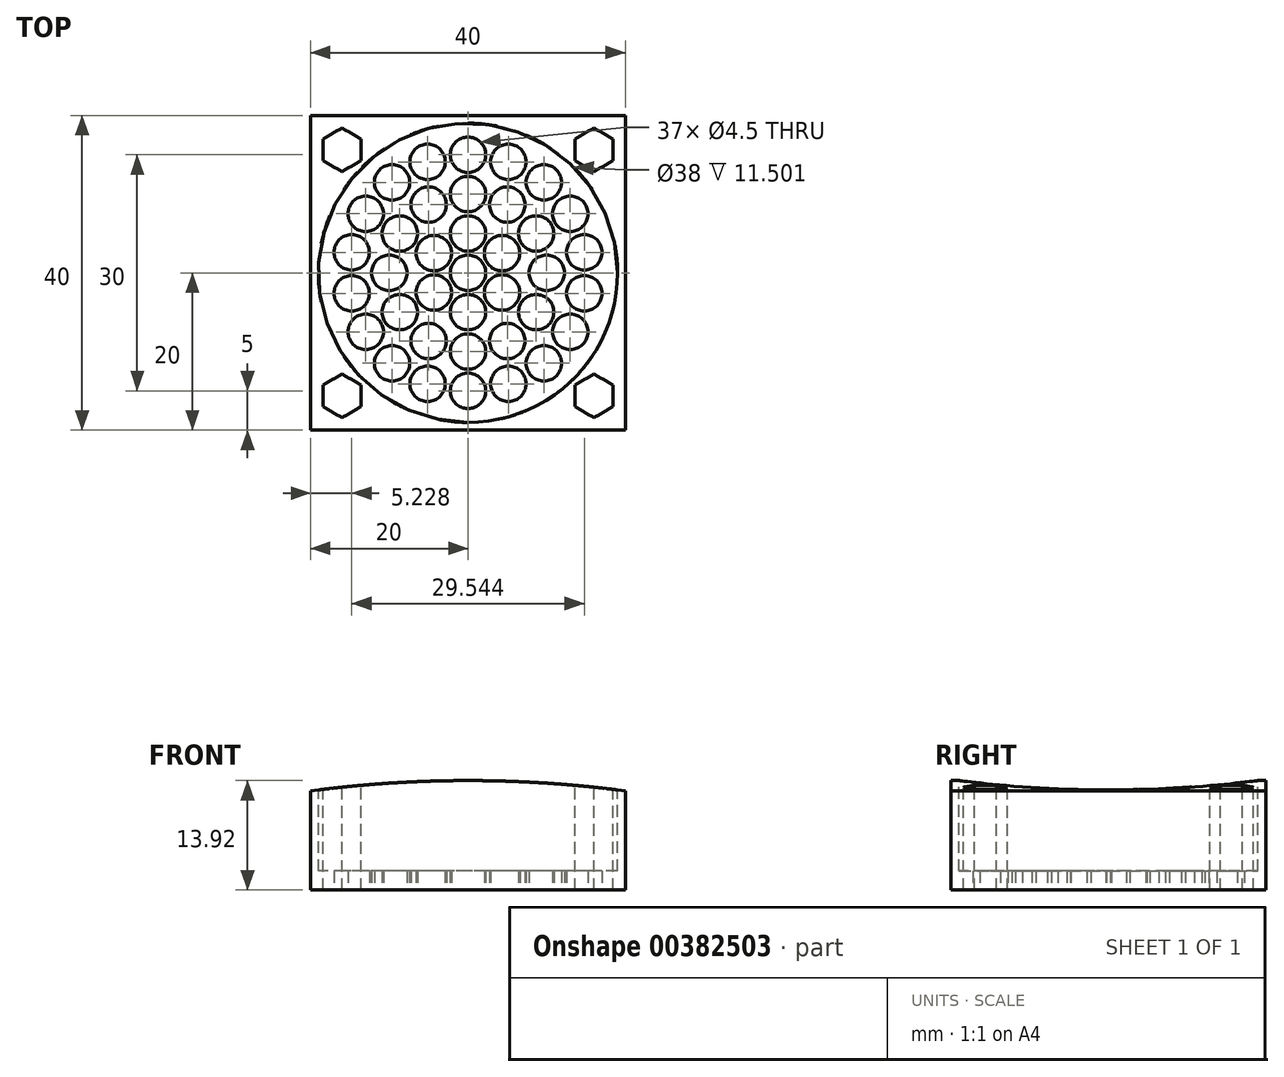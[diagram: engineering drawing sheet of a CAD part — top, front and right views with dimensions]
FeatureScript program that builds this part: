
annotation { "Feature Type Name" : "Feature", "Feature Type Description" : "" }
export const myFeature = defineFeature(function(context is Context, id is Id, definition is map)
    precondition{}
    {
        {
            var Q0;
            Q0=qCreatedBy(makeId("Top.planeOp"),FACE);
            var sketch = newSketch(context, id + "F0", { "sketchPlane" : qUnion([Q0])});
            skLineSegment(sketch, "E0.bottom", {"start": v(-20, 20) * mm, "end": v(20, 20) * mm});
            skLineSegment(sketch, "E0.top", {"start": v(-20, -20) * mm, "end": v(20, -20) * mm});
            skLineSegment(sketch, "E0.left", {"start": v(-20, 20) * mm, "end": v(-20, -20) * mm});
            skLineSegment(sketch, "E0.right", {"start": v(20, 20) * mm, "end": v(20, -20) * mm});
            skSolve(sketch);
        }
        {
            var Q0;
            Q0 = qSketchRegion(id + "F0", true);
            extrude(context, id + "F1", {"entities" : qUnion([Q0]), "depth" : 13.92 * mm});
        }
        {
            var Q0;
            Q0=makeQuery(id+"F1.opExtrude","CAP_FACE",FACE,{"disambiguationData":[OSD([sQuery(id+"F0.wireOp",EDGE,"E0.bottom"),sQuery(id+"F0.wireOp",EDGE,"E0.top"),sQuery(id+"F0.wireOp",EDGE,"E0.left"),sQuery(id+"F0.wireOp",EDGE,"E0.right")])],"isStart":false});
            var sketch = newSketch(context, id + "F2", { "sketchPlane" : qUnion([Q0])});
            skLineSegment(sketch, "E1", {"start": v(-16, 18.4) * mm, "end": v(-18.4, 17.01) * mm});
            skLineSegment(sketch, "E2", {"start": v(-18.4, 17.01) * mm, "end": v(-18.4, 14.24) * mm});
            skLineSegment(sketch, "E3", {"start": v(-18.4, 14.24) * mm, "end": v(-16, 12.86) * mm});
            skLineSegment(sketch, "E4", {"start": v(-16, 12.86) * mm, "end": v(-13.6, 14.24) * mm});
            skLineSegment(sketch, "E5", {"start": v(-13.6, 14.24) * mm, "end": v(-13.6, 17.01) * mm});
            skLineSegment(sketch, "E6", {"start": v(-13.6, 17.01) * mm, "end": v(-16, 18.4) * mm});
            skLineSegment(sketch, "E7.MirrorCS", {"start": v(13.6, 14.24) * mm, "end": v(13.6, 17.01) * mm});
            skLineSegment(sketch, "E8.MirrorCS", {"start": v(18.4, 17.01) * mm, "end": v(18.4, 14.24) * mm});
            skLineSegment(sketch, "E9.MirrorCS", {"start": v(16, 18.4) * mm, "end": v(18.4, 17.01) * mm});
            skLineSegment(sketch, "E10.MirrorCS", {"start": v(18.4, 14.24) * mm, "end": v(16, 12.86) * mm});
            skLineSegment(sketch, "E11.MirrorCS", {"start": v(13.6, 17.01) * mm, "end": v(16, 18.4) * mm});
            skLineSegment(sketch, "E12.MirrorCS", {"start": v(16, 12.86) * mm, "end": v(13.6, 14.24) * mm});
            skLineSegment(sketch, "E13.MirrorCS", {"start": v(-13.6, -14.24) * mm, "end": v(-13.6, -17.01) * mm});
            skLineSegment(sketch, "E14.MirrorCS", {"start": v(-18.4, -17.01) * mm, "end": v(-18.4, -14.24) * mm});
            skLineSegment(sketch, "E15.MirrorCS", {"start": v(16, -12.86) * mm, "end": v(13.6, -14.24) * mm});
            skLineSegment(sketch, "E16.MirrorCS", {"start": v(18.4, -14.24) * mm, "end": v(16, -12.86) * mm});
            skLineSegment(sketch, "E17.MirrorCS", {"start": v(16, -18.4) * mm, "end": v(18.4, -17.01) * mm});
            skLineSegment(sketch, "E18.MirrorCS", {"start": v(-13.6, -17.01) * mm, "end": v(-16, -18.4) * mm});
            skLineSegment(sketch, "E19.MirrorCS", {"start": v(-16, -18.4) * mm, "end": v(-18.4, -17.01) * mm});
            skLineSegment(sketch, "E20.MirrorCS", {"start": v(13.6, -14.24) * mm, "end": v(13.6, -17.01) * mm});
            skLineSegment(sketch, "E21.MirrorCS", {"start": v(18.4, -17.01) * mm, "end": v(18.4, -14.24) * mm});
            skLineSegment(sketch, "E22.MirrorCS", {"start": v(-16, -12.86) * mm, "end": v(-13.6, -14.24) * mm});
            skLineSegment(sketch, "E23.MirrorCS", {"start": v(-18.4, -14.24) * mm, "end": v(-16, -12.86) * mm});
            skLineSegment(sketch, "E24.MirrorCS", {"start": v(13.6, -17.01) * mm, "end": v(16, -18.4) * mm});
            skSolve(sketch);
        }
        {
            var Q0;
            Q0 = qSketchRegion(id + "F2", true);
            extrude(context, id + "F3", {"entities" : qUnion([Q0]), "operationType" : NewBodyOperationType.REMOVE, "oppositeDirection" : true, "depth" : 25 * mm});
        }
        {
            var Q0;
            Q0=makeQuery(id+"F1.opExtrude","CAP_FACE",FACE,{"disambiguationData":[OSD([sQuery(id+"F0.wireOp",EDGE,"E0.bottom"),sQuery(id+"F0.wireOp",EDGE,"E0.top"),sQuery(id+"F0.wireOp",EDGE,"E0.left"),sQuery(id+"F0.wireOp",EDGE,"E0.right")])],"isStart":false});
            var sketch = newSketch(context, id + "F4", { "sketchPlane" : qUnion([Q0])});
            skCircle(sketch, "E25", {"center": v(0, 0) * mm, "radius": 19 * mm});
            skSolve(sketch);
        }
        {
            var Q0;
            Q0 = qSketchRegion(id + "F4", true);
            extrude(context, id + "F5", {"entities" : qUnion([Q0]), "operationType" : NewBodyOperationType.REMOVE, "oppositeDirection" : true, "depth" : 11.5 * mm});
        }
        {
            var Q0;
            Q0=makeQuery(id+"F1.opExtrude","SWEPT_FACE",FACE,{"disambiguationData":[OSD([sQuery(id+"F0.wireOp",EDGE,"E0.bottom")])]});
            var sketch = newSketch(context, id + "F6", { "sketchPlane" : qUnion([Q0])});
            skArc(sketch, "E26", {"start": v(20, 12.6) * mm, "mid": v(0, 13.92) * mm, "end": v(-20, 12.6) * mm});
            skLineSegment(sketch, "E27", {"start": v(-20, 12.6) * mm, "end": v(-20, 13.92) * mm});
            skLineSegment(sketch, "E28", {"start": v(-20, 13.92) * mm, "end": v(20, 13.92) * mm});
            skLineSegment(sketch, "E29", {"start": v(20, 13.92) * mm, "end": v(20, 12.6) * mm});
            skSolve(sketch);
        }
        {
            var Q0;
            Q0 = qSketchRegion(id + "F6", true);
            extrude(context, id + "F7", {"entities" : qUnion([Q0]), "operationType" : NewBodyOperationType.REMOVE, "oppositeDirection" : true, "depth" : 50 * mm});
        }
        {
            var Q0;
            Q0=makeQuery(id+"F1.opExtrude","CAP_FACE",FACE,{"disambiguationData":[OSD([sQuery(id+"F0.wireOp",EDGE,"E0.bottom"),sQuery(id+"F0.wireOp",EDGE,"E0.top"),sQuery(id+"F0.wireOp",EDGE,"E0.left"),sQuery(id+"F0.wireOp",EDGE,"E0.right")])],"isStart":true});
            var sketch = newSketch(context, id + "F8", { "sketchPlane" : qUnion([Q0])});
            skCircle(sketch, "E30", {"center": v(0, 0) * mm, "radius": 2.25 * mm});
            skCircle(sketch, "E31", {"center": v(0, 5) * mm, "radius": 2.25 * mm});
            skCircle(sketch, "E32.1.0", {"center": v(-4.33, 2.5) * mm, "radius": 2.25 * mm});
            skCircle(sketch, "E32.2.0", {"center": v(-4.33, -2.5) * mm, "radius": 2.25 * mm});
            skCircle(sketch, "E32.3.0", {"center": v(0, -5) * mm, "radius": 2.25 * mm});
            skCircle(sketch, "E32.4.0", {"center": v(4.33, -2.5) * mm, "radius": 2.25 * mm});
            skCircle(sketch, "E32.5.0", {"center": v(4.33, 2.5) * mm, "radius": 2.25 * mm});
            skCircle(sketch, "E33", {"center": v(0, 10) * mm, "radius": 2.25 * mm});
            skCircle(sketch, "E34", {"center": v(0, 15) * mm, "radius": 2.25 * mm});
            skCircle(sketch, "E35.1.0", {"center": v(-5.13, 14.1) * mm, "radius": 2.25 * mm});
            skCircle(sketch, "E35.2.0", {"center": v(-9.64, 11.5) * mm, "radius": 2.25 * mm});
            skCircle(sketch, "E35.3.0", {"center": v(-13, 7.5) * mm, "radius": 2.25 * mm});
            skCircle(sketch, "E35.4.0", {"center": v(-14.77, 2.6) * mm, "radius": 2.25 * mm});
            skCircle(sketch, "E35.5.0", {"center": v(-14.77, -2.6) * mm, "radius": 2.25 * mm});
            skCircle(sketch, "E35.6.0", {"center": v(-13, -7.5) * mm, "radius": 2.25 * mm});
            skCircle(sketch, "E35.7.0", {"center": v(-9.64, -11.5) * mm, "radius": 2.25 * mm});
            skCircle(sketch, "E35.8.0", {"center": v(-5.13, -14.1) * mm, "radius": 2.25 * mm});
            skCircle(sketch, "E35.9.0", {"center": v(0, -15) * mm, "radius": 2.25 * mm});
            skCircle(sketch, "E35.10.0", {"center": v(5.13, -14.1) * mm, "radius": 2.25 * mm});
            skCircle(sketch, "E35.11.0", {"center": v(9.64, -11.5) * mm, "radius": 2.25 * mm});
            skCircle(sketch, "E35.12.0", {"center": v(13, -7.5) * mm, "radius": 2.25 * mm});
            skCircle(sketch, "E35.13.0", {"center": v(14.77, -2.6) * mm, "radius": 2.25 * mm});
            skCircle(sketch, "E35.14.0", {"center": v(14.77, 2.6) * mm, "radius": 2.25 * mm});
            skCircle(sketch, "E35.15.0", {"center": v(13, 7.5) * mm, "radius": 2.25 * mm});
            skCircle(sketch, "E35.16.0", {"center": v(9.64, 11.5) * mm, "radius": 2.25 * mm});
            skCircle(sketch, "E35.17.0", {"center": v(5.13, 14.1) * mm, "radius": 2.25 * mm});
            skCircle(sketch, "E36.1.0", {"center": v(-5, 8.66) * mm, "radius": 2.25 * mm});
            skCircle(sketch, "E36.2.0", {"center": v(-8.66, 5) * mm, "radius": 2.25 * mm});
            skCircle(sketch, "E36.3.0", {"center": v(-10, 0) * mm, "radius": 2.25 * mm});
            skCircle(sketch, "E36.4.0", {"center": v(-8.66, -5) * mm, "radius": 2.25 * mm});
            skCircle(sketch, "E36.5.0", {"center": v(-5, -8.66) * mm, "radius": 2.25 * mm});
            skCircle(sketch, "E36.6.0", {"center": v(0, -10) * mm, "radius": 2.25 * mm});
            skCircle(sketch, "E36.7.0", {"center": v(5, -8.66) * mm, "radius": 2.25 * mm});
            skCircle(sketch, "E36.8.0", {"center": v(8.66, -5) * mm, "radius": 2.25 * mm});
            skCircle(sketch, "E36.9.0", {"center": v(10, 0) * mm, "radius": 2.25 * mm});
            skCircle(sketch, "E36.10.0", {"center": v(8.66, 5) * mm, "radius": 2.25 * mm});
            skCircle(sketch, "E36.11.0", {"center": v(5, 8.66) * mm, "radius": 2.25 * mm});
            skSolve(sketch);
        }
        {
            var Q0;
            Q0 = qSketchRegion(id + "F8", true);
            extrude(context, id + "F9", {"entities" : qUnion([Q0]), "operationType" : NewBodyOperationType.REMOVE, "oppositeDirection" : true, "depth" : 25 * mm});
        }
    });
